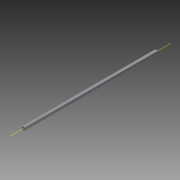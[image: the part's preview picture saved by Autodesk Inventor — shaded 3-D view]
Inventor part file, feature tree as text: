
AUTODESK INVENTOR PART (.ipt)
format: ipt  version: 2015 (Build 190159000, 159)  size: 156,160 bytes
history: native  units: in
note: dims shown in document units (in); Inventor stores cm internally (conversion verified against a paired STEP export)
features: other x5, extrude x1, imported_body x1, sketch x1
ambient origin geometry x8: Origin, YZ Plane, XZ Plane, XY Plane, X Axis, Y Axis, Z Axis, Center Point
bodies: Body1 (feature_tree)
feature tree (8):
  parser-record x1  (decoder bookkeeping rows leaked as tree rows — omitted from the tree; the rows remain in map.json)
  other  "Shaft"
  extrude  "length cut"  Depth=6.0in
  other  "front plane"
  imported_body  "Base1"
  sketch  "Sketch1"  dims[d1=0.0in d2=6.0in d3=0.0in d4=0.0in d5=0.0in]
  other  "main axis"
  other  "back plane"
